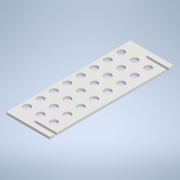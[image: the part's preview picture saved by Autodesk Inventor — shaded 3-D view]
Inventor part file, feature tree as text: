
AUTODESK INVENTOR PART (.ipt)
format: ipt  version: 2020 (Build 240168000, 168)  size: 306,176 bytes
history: native  units: in
note: dims shown in document units (in); Inventor stores cm internally (conversion verified against a paired STEP export)
features: extrude x1, sketch x1
ambient origin geometry x8: Origin, YZ Plane, XZ Plane, XY Plane, X Axis, Y Axis, Z Axis, Center Point
bodies: Solid1 (feature_tree)
feature tree (2):
  extrude  "Extrusion1"  Depth=12.7843in
  sketch  "Sketch1"  dims[d0=4.445in d1=12.7843in d7=0.7188in d8=1.75in d10=1.388in d11=1.388in d12=1.388in d13=1.388in d14=1.388in d15=1.388in d16=1.388in d17=1.388in d21=0.7188in d22=1.388in d23=1.388in d24=1.388in d25=1.388in d26=1.388in d27=1.388in d28=1.388in d31=0.25in d32=0.0in d34=0.7188in d35=1.388in d36=1.388in d37=1.388in d38=1.388in d39=1.388in d40=1.388in d41=1.388in d42=1.388in d43=0.5845in d48=0.23in d49=0.23in d50=2.2225in d51=0.5in d52=0.5in d53=5.6981in d54=0.05in]
